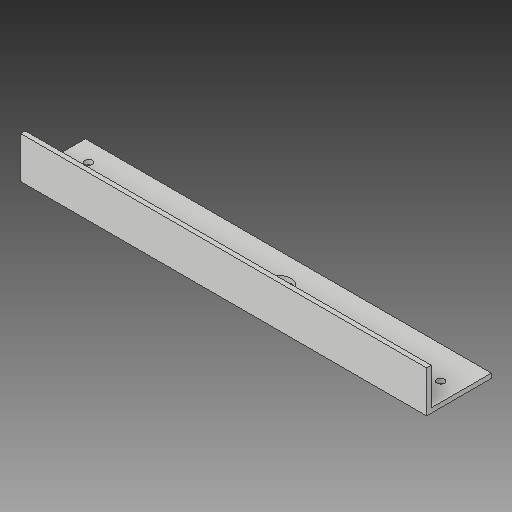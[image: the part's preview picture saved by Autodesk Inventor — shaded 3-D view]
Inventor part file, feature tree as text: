
AUTODESK INVENTOR PART (.ipt)
format: ipt  version: 2018 (Build 220112000, 112)  size: 102,912 bytes
history: native  units: in
note: dims shown in document units (in); Inventor stores cm internally (conversion verified against a paired STEP export)
features: sketch x4, other x3
ambient origin geometry x8: Origin, YZ Plane, XZ Plane, XY Plane, X Axis, Y Axis, Z Axis, Center Point
bodies: Solid1 (feature_tree)
feature tree (7):
  other  "angle iron with  holes 2_MIR.ipt"
  other  "Solid1::angle iron with  holes 2_MIR.ipt"
  other  "TaggingFeature1"
  sketch  "Sketch1"  dims[d0=0.3937in]
  sketch  "Sketch2"
  sketch  "Sketch3"
  sketch  "Sketch4"
